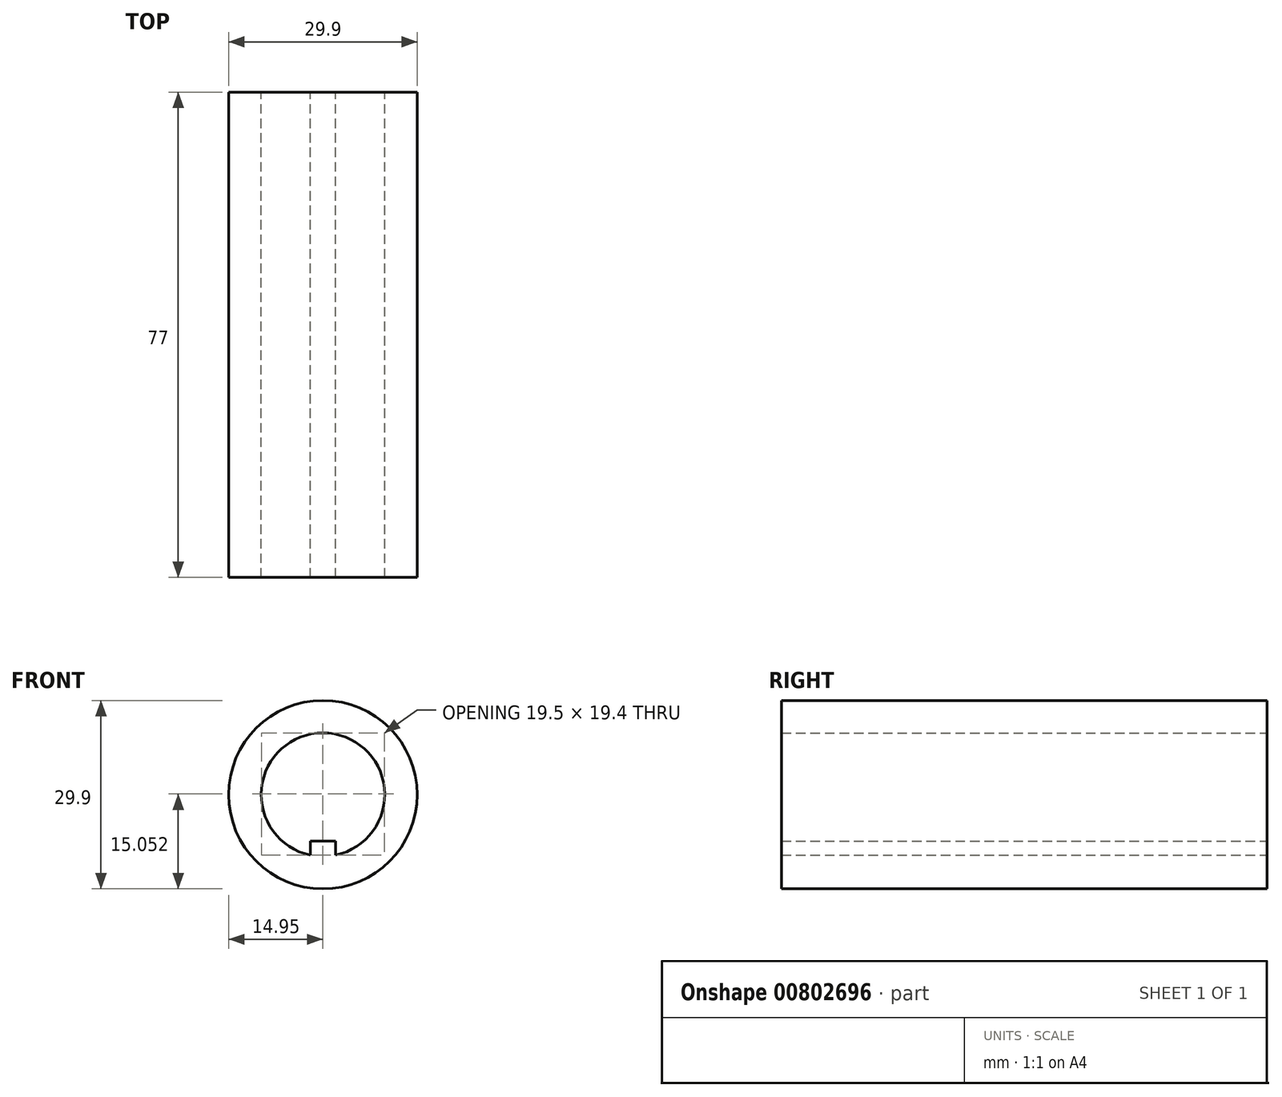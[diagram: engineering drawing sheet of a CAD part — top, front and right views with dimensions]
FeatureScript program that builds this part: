
annotation { "Feature Type Name" : "Feature", "Feature Type Description" : "" }
export const myFeature = defineFeature(function(context is Context, id is Id, definition is map)
    precondition{}
    {
        {
            var Q0;
            Q0=qCreatedBy(makeId("Front.planeOp"),FACE);
            var sketch = newSketch(context, id + "F0", { "sketchPlane" : qUnion([Q0])});
            skCircle(sketch, "E0", {"center": v(0, 0) * mm, "radius": 14.95 * mm});
            skArc(sketch, "E1", {"start": v(1.99, -9.6) * mm, "mid": v(0, 9.8) * mm, "end": v(-1.99, -9.6) * mm});
            skLineSegment(sketch, "E2", {"start": v(1.99, -9.6) * mm, "end": v(1.99, -7.35) * mm});
            skLineSegment(sketch, "E3", {"start": v(1.99, -7.35) * mm, "end": v(-2.01, -7.35) * mm});
            skLineSegment(sketch, "E4", {"start": v(-1.99, -9.6) * mm, "end": v(-2.01, -7.35) * mm});
            skPoint(sketch, "E5.orphan", {"position": v(0, -9.8) * mm});
            skSolve(sketch);
        }
        {
            var Q0;
            Q0=makeQuery(id+"F0.imprint","IMPRINT",FACE,{"disambiguationData":[TD([[makeQuery(id+"F0.imprint","IMPRINT",EDGE,{"derivedFrom":sQuery(id+"F0.wireOp",EDGE,"Evy0lBa0-QF4y-qAFu-Zf10-gi5ICgwZNrtD")}),-1.0]])]});
            var Q1;
            Q1=makeQuery(id+"F0.imprint","IMPRINT",FACE,{"disambiguationData":[TD([[makeQuery(id+"F0.imprint","IMPRINT",EDGE,{"derivedFrom":sQuery(id+"F0.wireOp",EDGE,"E0")}),1.0]])]});
            extrude(context, id + "F1", {"entities" : qUnion([Q0, Q1]), "depth" : 77 * mm, "offsetDistance" : 25 * mm});
        }
    });
